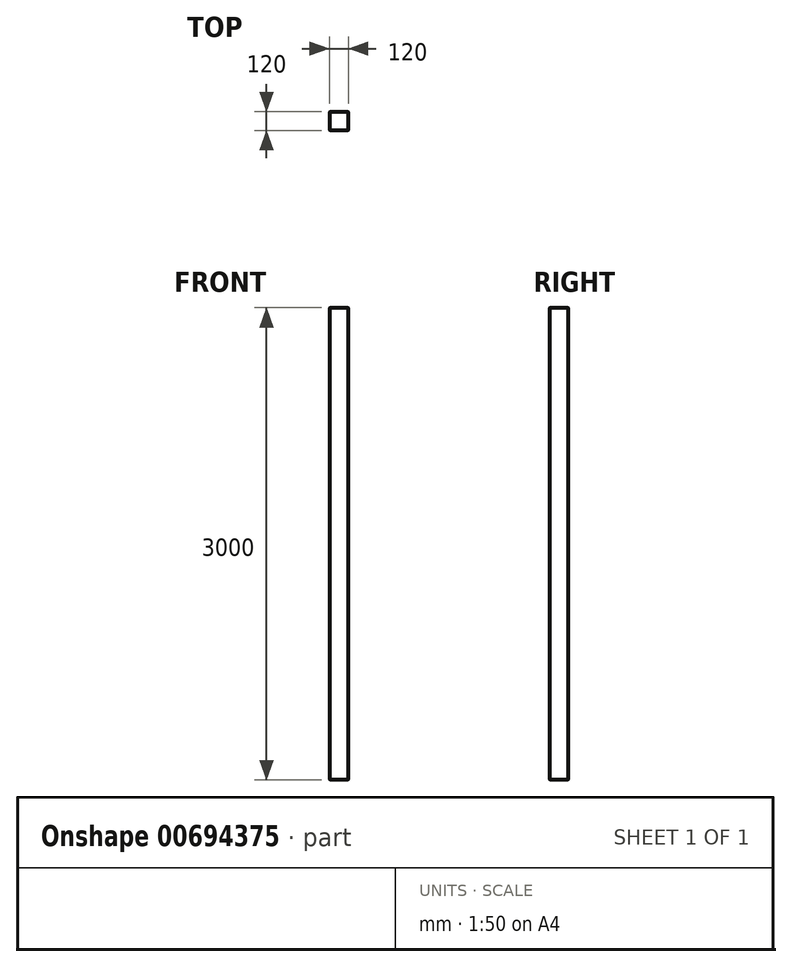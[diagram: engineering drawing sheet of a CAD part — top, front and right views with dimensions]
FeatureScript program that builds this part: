
annotation { "Feature Type Name" : "Feature", "Feature Type Description" : "" }
export const myFeature = defineFeature(function(context is Context, id is Id, definition is map)
    precondition{}
    {
        {
            var Q0;
            Q0=qCreatedBy(makeId("Top.planeOp"),FACE);
            var sketch = newSketch(context, id + "F0", { "sketchPlane" : qUnion([Q0])});
            skLineSegment(sketch, "E0.bottom", {"start": v(-64.14, -60.84) * mm, "end": v(55.86, -60.84) * mm});
            skLineSegment(sketch, "E0.top", {"start": v(-64.14, 59.16) * mm, "end": v(55.86, 59.16) * mm});
            skLineSegment(sketch, "E0.left", {"start": v(-64.14, -60.84) * mm, "end": v(-64.14, 59.16) * mm});
            skLineSegment(sketch, "E0.right", {"start": v(55.86, -60.84) * mm, "end": v(55.86, 59.16) * mm});
            skSolve(sketch);
        }
        {
            var Q0;
            Q0 = qSketchRegion(id + "F0", true);
            extrude(context, id + "F1", {"entities" : qUnion([Q0]), "depth" : 3000 * mm, "offsetDistance" : 25 * mm});
        }
        {
            var Q0;
            Q0=makeQuery(id+"F1.opExtrude","CAP_EDGE",EDGE,{"disambiguationData":[OSD([sQuery(id+"F0.wireOp",EDGE,"E0.left")])],"isStart":false});
            var Q1;
            Q1=makeQuery(id+"F1.opExtrude","CAP_EDGE",EDGE,{"disambiguationData":[OSD([sQuery(id+"F0.wireOp",EDGE,"E0.bottom")])],"isStart":false});
            var Q2;
            Q2=makeQuery(id+"F1.opExtrude","CAP_EDGE",EDGE,{"disambiguationData":[OSD([sQuery(id+"F0.wireOp",EDGE,"E0.right")])],"isStart":false});
            var Q3;
            Q3=makeQuery(id+"F1.opExtrude","CAP_EDGE",EDGE,{"disambiguationData":[OSD([sQuery(id+"F0.wireOp",EDGE,"E0.top")])],"isStart":false});
            var Q4;
            Q4=makeQuery(id+"F1.opExtrude","SWEPT_EDGE",EDGE,{"disambiguationData":[OSD([sQuery(id+"F0.wireOp",EDGE,"E0.top"),sQuery(id+"F0.wireOp",EDGE,"E0.right")])]});
            var Q5;
            Q5=makeQuery(id+"F1.opExtrude","SWEPT_EDGE",EDGE,{"disambiguationData":[OSD([sQuery(id+"F0.wireOp",EDGE,"E0.bottom"),sQuery(id+"F0.wireOp",EDGE,"E0.right")])]});
            var Q6;
            Q6=makeQuery(id+"F1.opExtrude","SWEPT_EDGE",EDGE,{"disambiguationData":[OSD([sQuery(id+"F0.wireOp",EDGE,"E0.bottom"),sQuery(id+"F0.wireOp",EDGE,"E0.left")])]});
            var Q7;
            Q7=makeQuery(id+"F1.opExtrude","CAP_EDGE",EDGE,{"disambiguationData":[OSD([sQuery(id+"F0.wireOp",EDGE,"E0.bottom")])],"isStart":true});
            var Q8;
            Q8=makeQuery(id+"F1.opExtrude","CAP_EDGE",EDGE,{"disambiguationData":[OSD([sQuery(id+"F0.wireOp",EDGE,"E0.right")])],"isStart":true});
            var Q9;
            Q9=makeQuery(id+"F1.opExtrude","SWEPT_EDGE",EDGE,{"disambiguationData":[OSD([sQuery(id+"F0.wireOp",EDGE,"E0.top"),sQuery(id+"F0.wireOp",EDGE,"E0.left")])]});
            var Q10;
            Q10=makeQuery(id+"F1.opExtrude","CAP_EDGE",EDGE,{"disambiguationData":[OSD([sQuery(id+"F0.wireOp",EDGE,"E0.top")])],"isStart":true});
            var Q11;
            Q11=makeQuery(id+"F1.opExtrude","CAP_EDGE",EDGE,{"disambiguationData":[OSD([sQuery(id+"F0.wireOp",EDGE,"E0.left")])],"isStart":true});
            chamfer(context, id + "F2", {"entities" : qUnion([Q0, Q1, Q2, Q3, Q4, Q5, Q6, Q7, Q8, Q9, Q10, Q11]), "width" : 3 * mm, "tangentPropagation" : true});
        }
    });
